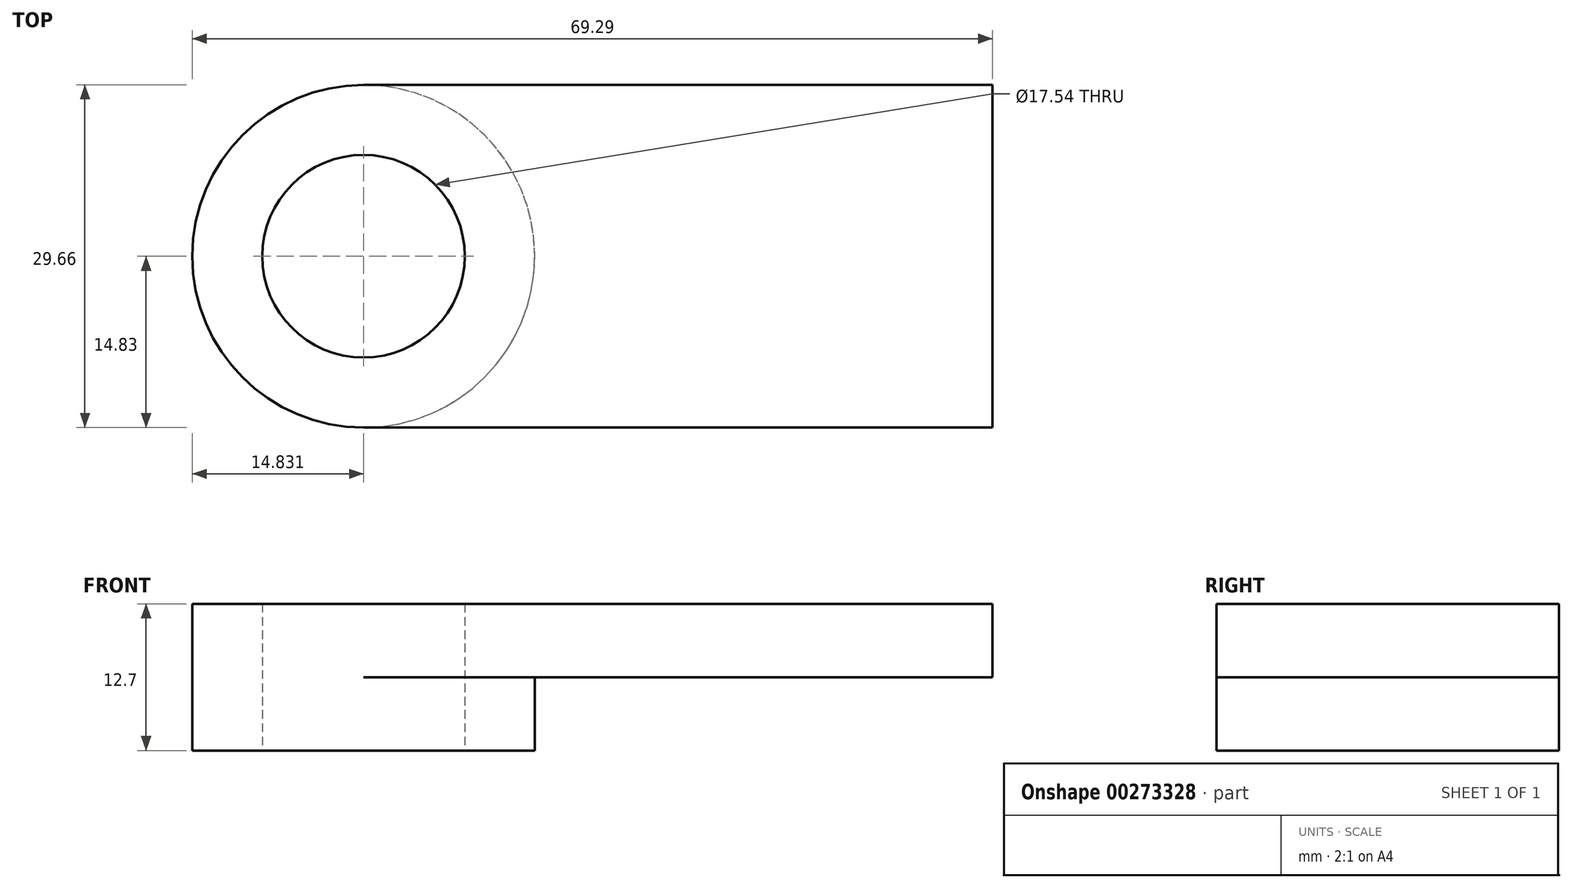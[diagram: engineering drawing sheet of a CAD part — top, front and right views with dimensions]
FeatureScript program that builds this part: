
annotation { "Feature Type Name" : "Feature", "Feature Type Description" : "" }
export const myFeature = defineFeature(function(context is Context, id is Id, definition is map)
    precondition{}
    {
        {
            var Q0;
            Q0=qCreatedBy(makeId("Top.planeOp"),FACE);
            var sketch = newSketch(context, id + "F0", { "sketchPlane" : qUnion([Q0])});
            skLineSegment(sketch, "E0.bottom", {"start": v(-27.23, 14.83) * mm, "end": v(27.23, 14.83) * mm});
            skLineSegment(sketch, "E0.top", {"start": v(-27.23, -14.83) * mm, "end": v(27.23, -14.83) * mm});
            skLineSegment(sketch, "E0.left", {"start": v(-27.23, 14.83) * mm, "end": v(-27.23, -14.83) * mm});
            skLineSegment(sketch, "E0.right", {"start": v(27.23, 14.83) * mm, "end": v(27.23, -14.83) * mm});
            skPoint(sketch, "E0.middle", {"position": v(0, 0) * mm});
            skCircle(sketch, "E1", {"center": v(-27.23, 0) * mm, "radius": 14.83 * mm});
            skCircle(sketch, "E2", {"center": v(-27.23, 0) * mm, "radius": 8.77 * mm});
            skSolve(sketch);
        }
        {
            var Q0;
            Q0 = qSketchRegion(id + "F0", true);
            extrude(context, id + "F1", {"entities" : qUnion([Q0]), "depth" : 6.35 * mm});
        }
        {
            var Q0;
            {var subQ1=sQuery(id+"F0.wireOp",EDGE,"E0.left");var subQ3=sQuery(id+"F0.wireOp",EDGE,"E2");var subQ4=makeQuery(id+"F0.imprint","INTERSECT",VERTEX,{"disambiguationData":[OD(0.0)],"derivedFrom":[subQ1,subQ3]});Q0=makeQuery(id+"F0.imprint","IMPRINT",FACE,{"disambiguationData":[TD([[makeQuery(id+"F0.imprint","IMPRINT",EDGE,{"disambiguationData":[TD([[subQ4,-1.0]])],"derivedFrom":subQ3}),-1.0]])]});}
            var Q1;
            {var subQ1=sQuery(id+"F0.wireOp",EDGE,"E0.left");var subQ3=sQuery(id+"F0.wireOp",EDGE,"E2");var subQ4=makeQuery(id+"F0.imprint","INTERSECT",VERTEX,{"disambiguationData":[OD(0.0)],"derivedFrom":[subQ1,subQ3]});Q1=makeQuery(id+"F0.imprint","IMPRINT",FACE,{"disambiguationData":[TD([[makeQuery(id+"F0.imprint","IMPRINT",EDGE,{"disambiguationData":[TD([[subQ4,1.0]])],"derivedFrom":subQ3}),-1.0]])]});}
            extrude(context, id + "F2", {"entities" : qUnion([Q0, Q1]), "operationType" : NewBodyOperationType.ADD, "oppositeDirection" : true, "depth" : 6.35 * mm});
        }
    });
